# Revit family: Vario-DP_rohový_DN010_RFA_2018
name_source: partatom
category: Pipe Accessories
revit_build: Autodesk Revit LT 2018 (Build: 20180329_1100(x64)
units: mm (PartAtom-declared; Revit-internal decimal feet)

## family parameters
Always vertical = Yes
Cut with Voids When Loaded = No
Part Type = Valve - Breaks Into
Round Connector Dimension = Use Diameter
Shared = No
Work Plane-Based = No

## types (3) — shared parameters
BBVIS = No
BX = 16 mm  [stored 0.0524934 ft]
BZ = 48 mm  [stored 0.15748 ft]
CAT = No
CAT0 = Yes
CenSd_RT0X_6 = 7 mm  [stored 0.0229659 ft]
CenSd_RT1_6 = 13 mm  [stored 0.0426509 ft]
DS1 = 15 mm  [stored 0.0492126 ft]
DS2 = 9 mm  [stored 0.0295276 ft]
DS3 = 4 mm  [stored 0.0131234 ft]
ENBL350 = No
H = 23 mm  [stored 0.0754593 ft]
HS = 16 mm  [stored 0.0524934 ft]
L1 = 8 mm  [stored 0.0262467 ft]
L1__ve = -8 mm  [stored -0.0262467 ft]
L2 = 13 mm  [stored 0.0426509 ft]
L2D_Min = 30 mm  [stored 0.0984252 ft]
L2__ve = -13 mm  [stored -0.0426509 ft]
LLDAndHLD = Yes
LLDONLY = Yes
MC Enable LOD 200 = No
MC Enable LOD 350 = No
MC Pressure Drop Maximum Value = 0.0 Pa
MC Pressure Drop Minimum Value = 0.0 Pa
MC Use Limits From Balancing Method = No
Manufacturer = Hydronix
QmdConnectorList = 301;D;302;D
RT0 = 10 mm  [stored 0.0328084 ft]
RT01 = 9 mm  [stored 0.0295276 ft]
RT0X = 9 mm  [stored 0.0295276 ft]
RT1 = 16 mm  [stored 0.0524934 ft]
RT2 = 11 mm  [stored 0.0360892 ft]
RT3 = 13 mm  [stored 0.0426509 ft]
RTX = 3 mm  [stored 0.00984252 ft]
RT_01 = 8 mm  [stored 0.0262467 ft]
SW = Yes
SW1 = Yes
SW11 = No
SW1_ENBL350 = No
SW1_LLDONLY = Yes
SW2 = No
SW22 = No
SW2_ENBL350 = No
SW2_LLDAndHLD = No
SW2_LLDONLY = No
SW_1 = Yes
SW_2 = No
Type Comments = Termostatický radiátorový ventil s integrovaným omezovačem průtoku; rohový; závitový, PN10; +0~+90°C; pracovní dp 15-70kPa; max. síla pohonu 120N; připojení hlavice: M30x1,5
URL = www.hydronix.cz
VIS0 = No
magiPartTypeId = 303
magiProductFamilyId = ec8f353124f843e091b2b692170bc8
zero-valued in all types: MC Throttling Maximum Value, MC Throttling Minimum Value

## per-type parameters (varying)
| type | BY | CenSd_RT22_6 | D | DT | Description | E | L | L2D | LD | LL | LL__ve | LX | L_ | MC Product Code | RT | RT02 | RT22 | RT4 | TL | TL__ve | W2D | magiProductId |
| Vario-DP rohový DN10 | 16 mm  [stored 0.0524934 ft] | 12 mm  [stored 0.0393701 ft] | 10 mm | 17 mm | Termostatický radiátorový ventil s omezovačem max. průtoku; DN10; rozsah nastavení omezovače max. průtok: 20-340l/h | 25 mm  [stored 0.082021 ft] | 42 mm | 42 mm | 52 mm  [stored 0.170604 ft] | 18 mm  [stored 0.0590551 ft] | -18 mm | 26 mm  [stored 0.0853018 ft] | 42 mm | VARIO-DP; rohový  DN10; (obj.č.: 161060100); dpmin=15kPa; dpmax: 70kPa;; rozsah nastavení 20-340l/h | 8 mm  [stored 0.0262467 ft] | 12 mm  [stored 0.0393701 ft] | 14 mm  [stored 0.0459318 ft] | 9 mm  [stored 0.0295276 ft] | 10 mm  [stored 0.0328084 ft] | -10 mm  [stored -0.0328084 ft] | 10 mm  [stored 0.0328084 ft] | 331eccc955f74f4b99483bcbe37d0b |
| Vario-DP rohový DN20 | 20 mm  [stored 0.0656168 ft] | 17 mm | 20 mm | 26 mm  [stored 0.0853018 ft] | Termostatický radiátorový ventil s omezovačem max. průtoku; DN20; rozsah nastavení omezovače max. průtok: 20-340l/h | 29 mm | 52 mm  [stored 0.170604 ft] | 52 mm  [stored 0.170604 ft] | 66 mm | 26 mm  [stored 0.0853018 ft] | -26 mm | 34 mm | 52 mm  [stored 0.170604 ft] | VARIO-DP; rohový  DN20; (obj.č.: 161080100); dpmin=15kPa; dpmax: 70kPa;; rozsah nastavení 20-340l/h | 13 mm  [stored 0.0426509 ft] | 17 mm | 20 mm  [stored 0.0656168 ft] | 14 mm  [stored 0.0459318 ft] | 15 mm  [stored 0.0492126 ft] | -15 mm  [stored -0.0492126 ft] | 20 mm  [stored 0.0656168 ft] | 65e9a6a884e34edd9d29bab7c484f5 |
| Vario-DP rohový DN15 | 16 mm  [stored 0.0524934 ft] | 15 mm  [stored 0.0492126 ft] | 15 mm | 21 mm  [stored 0.0688976 ft] | Termostatický radiátorový ventil s omezovačem max. průtoku; DN15; rozsah nastavení omezovače max. průtok: 20-340l/h | 26 mm  [stored 0.0853018 ft] | 45 mm | 45 mm | 58 mm | 21 mm  [stored 0.0688976 ft] | -21 mm | 29 mm | 45 mm | VARIO-DP; rohový  DN15; (obj.č.: 161070100); dpmin=15kPa; dpmax: 70kPa;; rozsah nastavení 20-340l/h | 11 mm  [stored 0.0360892 ft] | 16 mm  [stored 0.0524934 ft] | 18 mm  [stored 0.0590551 ft] | 11 mm  [stored 0.0360892 ft] | 13 mm  [stored 0.0426509 ft] | -13 mm  [stored -0.0426509 ft] | 15 mm  [stored 0.0492126 ft] | dd87fb7248b346b8ab3b7922b0665a |

note: [stored X ft] marks values corroborated as IEEE doubles in the binary element streams (Revit-internal decimal feet)

## geometry (parser evidence)
native form markers: Sweep x17
no freeform markers — native parametric forms only
